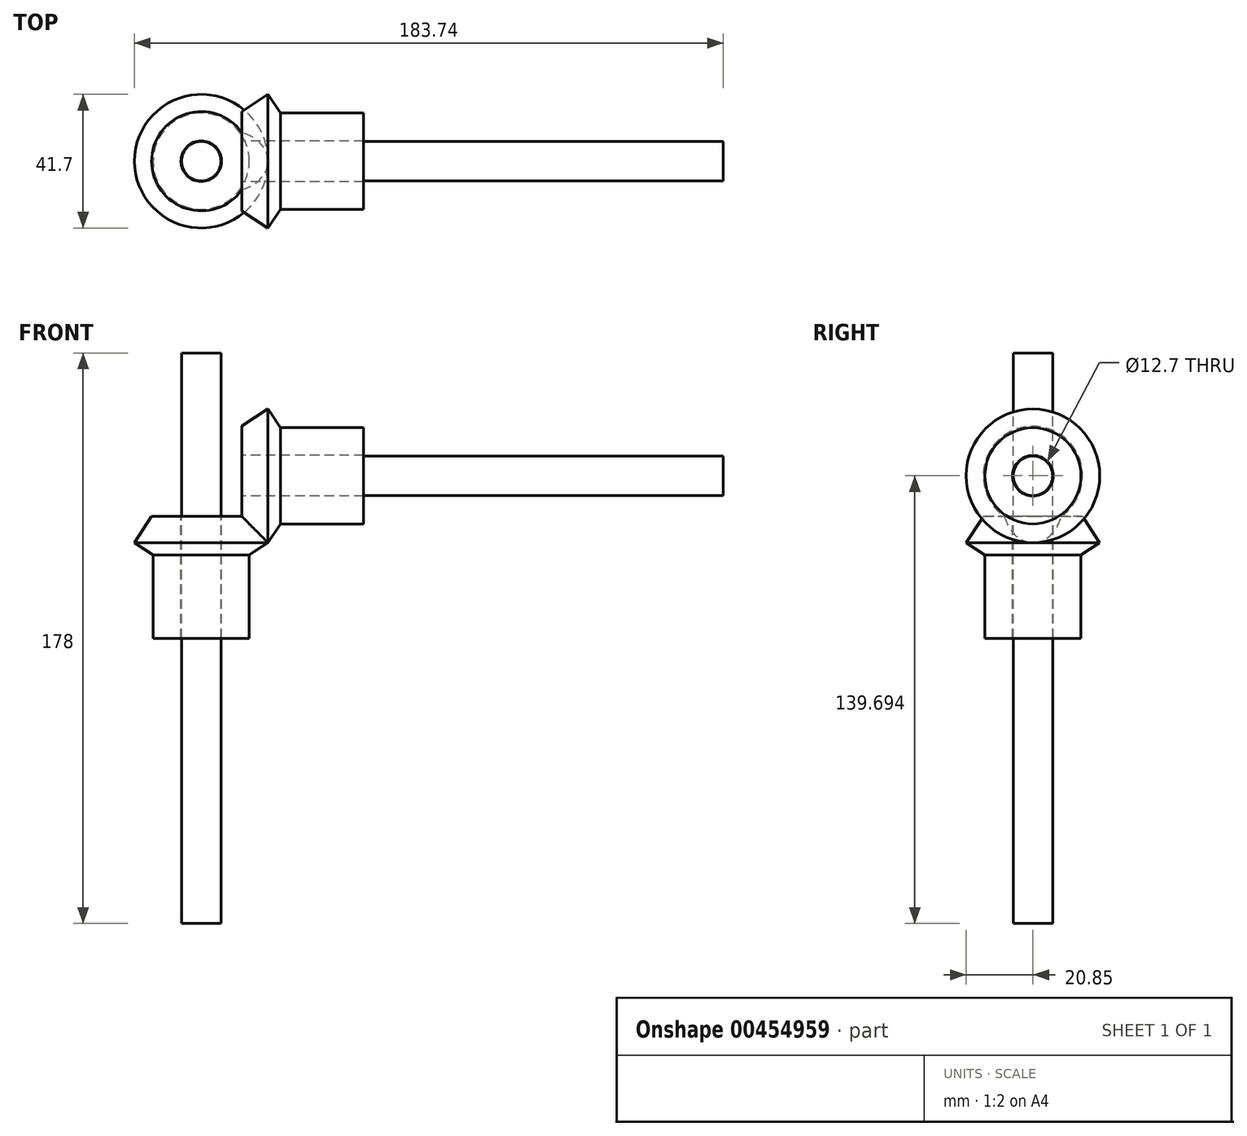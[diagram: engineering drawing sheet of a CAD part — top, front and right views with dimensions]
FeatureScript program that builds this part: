
annotation { "Feature Type Name" : "Feature", "Feature Type Description" : "" }
export const myFeature = defineFeature(function(context is Context, id is Id, definition is map)
    precondition{}
    {
        {
            var Q0;
            Q0=qCreatedBy(makeId("Front.planeOp"),FACE);
            var sketch = newSketch(context, id + "F0", { "sketchPlane" : qUnion([Q0])});
            skLineSegment(sketch, "E0", {"start": v(-6.35, 0) * mm, "end": v(-15, 0) * mm});
            skLineSegment(sketch, "E1", {"start": v(-15, 0) * mm, "end": v(-15, 13) * mm});
            skLineSegment(sketch, "E2", {"start": v(-15, 13) * mm, "end": v(-20.85, 16.84) * mm});
            skLineSegment(sketch, "E3", {"start": v(-20.85, 16.84) * mm, "end": v(-15.5, 25) * mm});
            skLineSegment(sketch, "E4", {"start": v(-6.35, 0) * mm, "end": v(-6.35, 25) * mm});
            skLineSegment(sketch, "E5", {"start": v(-15.5, 25) * mm, "end": v(-6.35, 25) * mm});
            skLineSegment(sketch, "E6", {"start": v(0, 40.5) * mm, "end": v(0, -1.9) * mm, "construction": true});
            skLineSegment(sketch, "E7", {"start": v(37.7, 31.34) * mm, "end": v(37.7, 22.7) * mm});
            skLineSegment(sketch, "E8", {"start": v(37.7, 22.7) * mm, "end": v(24.7, 22.7) * mm});
            skLineSegment(sketch, "E9", {"start": v(24.7, 22.7) * mm, "end": v(20.85, 16.84) * mm});
            skLineSegment(sketch, "E10", {"start": v(20.85, 16.84) * mm, "end": v(12.7, 22.2) * mm});
            skLineSegment(sketch, "E11", {"start": v(37.7, 31.34) * mm, "end": v(12.7, 31.34) * mm});
            skLineSegment(sketch, "E12", {"start": v(12.7, 22.2) * mm, "end": v(12.7, 31.34) * mm});
            skLineSegment(sketch, "E13", {"start": v(-2.8, 37.7) * mm, "end": v(39.6, 37.7) * mm, "construction": true});
            skSolve(sketch);
        }
        {
            var Q0;
            Q0=makeQuery(id+"F0.imprint","IMPRINT",FACE,{"disambiguationData":[TD([[makeQuery(id+"F0.imprint","IMPRINT",EDGE,{"derivedFrom":sQuery(id+"F0.wireOp",EDGE,"E0")}),-1.0]])]});
            var Q1;
            Q1=sQuery(id+"F0.wireOp",EDGE,"E6");
            revolve(context, id + "F1", {"entities" : qUnion([Q0]), "axis" : qUnion([Q1]), "revolveType" : RevolveType.FULL});
        }
        {
            var Q0;
            Q0=makeQuery(id+"F0.imprint","IMPRINT",FACE,{"disambiguationData":[TD([[makeQuery(id+"F0.imprint","IMPRINT",EDGE,{"derivedFrom":sQuery(id+"F0.wireOp",EDGE,"E7")}),-1.0]])]});
            var Q1;
            Q1=sQuery(id+"F0.wireOp",EDGE,"E13");
            revolve(context, id + "F2", {"operationType" : NewBodyOperationType.ADD, "entities" : qUnion([Q0]), "axis" : qUnion([Q1]), "revolveType" : RevolveType.FULL});
        }
        {
            var Q0;
            Q0=makeQuery(id+"F2.opRevolve","SWEPT_FACE",FACE,{"disambiguationData":[OSD([sQuery(id+"F0.wireOp",EDGE,"E7")])]});
            extrude(context, id + "F3", {"entities" : qUnion([Q0]), "operationType" : NewBodyOperationType.ADD, "depth" : 13 * mm});
        }
        {
            var Q0;
            Q0=makeQuery(id+"F1.opRevolve","SWEPT_FACE",FACE,{"disambiguationData":[OSD([sQuery(id+"F0.wireOp",EDGE,"E0")])]});
            extrude(context, id + "F4", {"entities" : qUnion([Q0]), "operationType" : NewBodyOperationType.ADD, "depth" : 13 * mm});
        }
        {
            var Q0;
            Q0=makeQuery(id+"F4.opExtrude","CAP_FACE",FACE,{"disambiguationData":[OSD([sQuery(id+"F0.wireOp",EDGE,"E0")])],"isStart":false});
            var sketch = newSketch(context, id + "F5", { "sketchPlane" : qUnion([Q0])});
            skCircle(sketch, "E14", {"center": v(0, 0) * mm, "radius": 6.14 * mm});
            skSolve(sketch);
        }
        {
            var Q0;
            Q0 = qSketchRegion(id + "F5", true);
            extrude(context, id + "F6", {"entities" : qUnion([Q0]), "endBound" : BoundingType.SYMMETRIC, "depth" : 178 * mm});
        }
        {
            var Q0;
            Q0=makeQuery(id+"F3.opExtrude","CAP_FACE",FACE,{"disambiguationData":[OSD([sQuery(id+"F0.wireOp",EDGE,"E7")])],"isStart":false});
            var sketch = newSketch(context, id + "F7", { "sketchPlane" : qUnion([Q0])});
            skCircle(sketch, "E15", {"center": v(0, 37.7) * mm, "radius": 6.14 * mm});
            skSolve(sketch);
        }
        {
            var Q0;
            Q0 = qSketchRegion(id + "F7", true);
            extrude(context, id + "F8", {"entities" : qUnion([Q0]), "depth" : 112.2 * mm});
        }
    });
